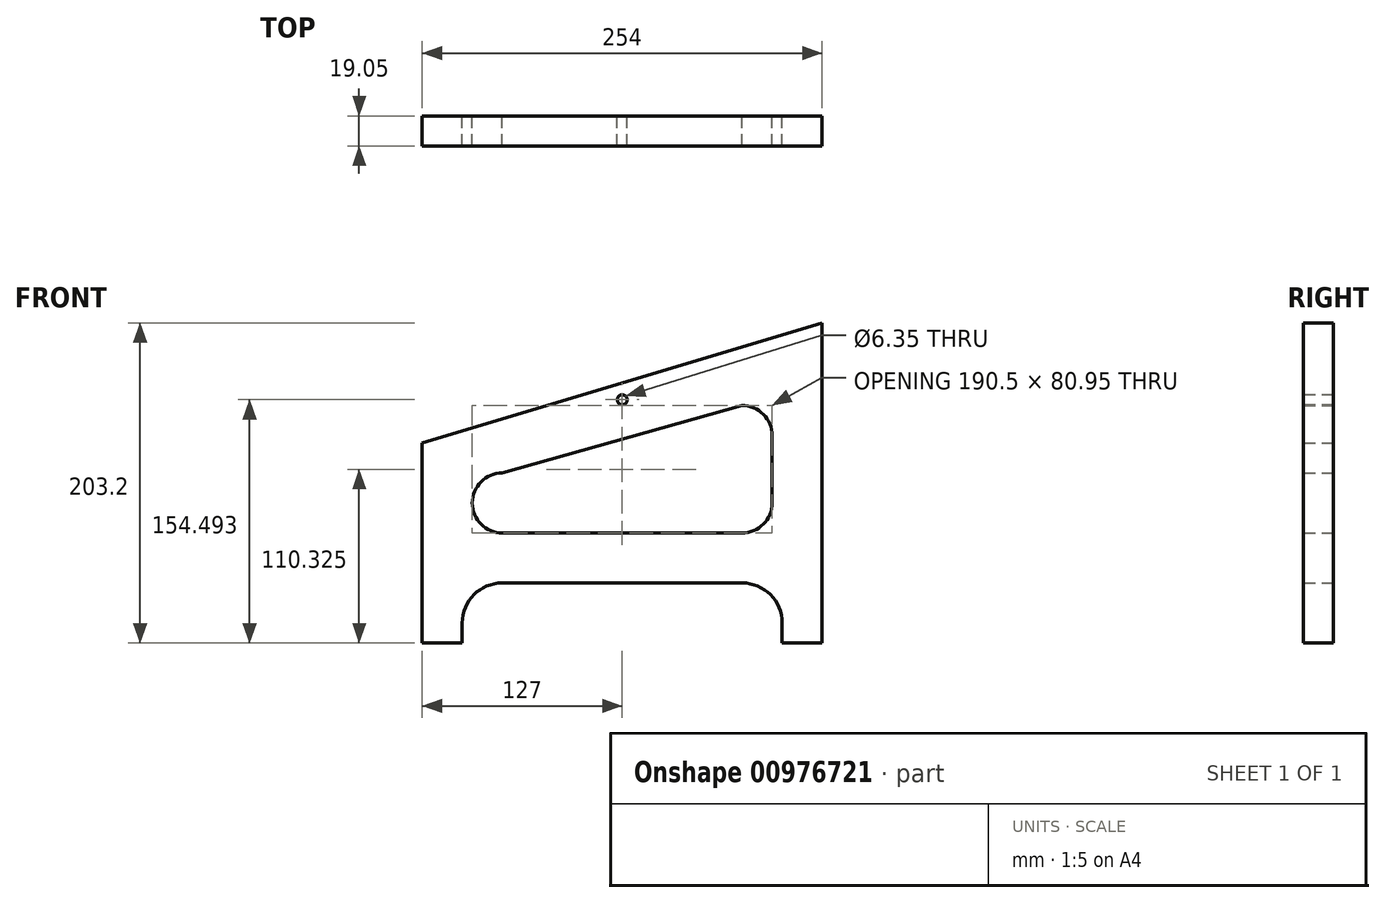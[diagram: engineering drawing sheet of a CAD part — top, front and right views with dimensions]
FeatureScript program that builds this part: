
annotation { "Feature Type Name" : "Feature", "Feature Type Description" : "" }
export const myFeature = defineFeature(function(context is Context, id is Id, definition is map)
    precondition{}
    {
        {
            var Q0;
            Q0=qCreatedBy(makeId("Front.planeOp"),FACE);
            var sketch = newSketch(context, id + "F0", { "sketchPlane" : qUnion([Q0])});
            skLineSegment(sketch, "E0", {"start": v(0, 0) * mm, "end": v(254, 0) * mm});
            skLineSegment(sketch, "E1", {"start": v(254, 0) * mm, "end": v(254, 203.2) * mm});
            skLineSegment(sketch, "E2", {"start": v(0, 0) * mm, "end": v(0, 127) * mm});
            skLineSegment(sketch, "E3", {"start": v(0, 127) * mm, "end": v(254, 203.2) * mm});
            skPoint(sketch, "E4", {"position": v(203.2, 12.7) * mm});
            skPoint(sketch, "E5", {"position": v(50.8, 12.7) * mm});
            skArc(sketch, "E6", {"start": v(50.8, 38.1) * mm, "mid": v(32.84, 30.66) * mm, "end": v(25.4, 12.7) * mm});
            skArc(sketch, "E7", {"start": v(228.6, 12.7) * mm, "mid": v(221.16, 30.66) * mm, "end": v(203.2, 38.1) * mm});
            skLineSegment(sketch, "E8", {"start": v(228.6, 12.7) * mm, "end": v(228.6, 0) * mm});
            skLineSegment(sketch, "E9", {"start": v(25.4, 12.7) * mm, "end": v(25.4, 0) * mm});
            skLineSegment(sketch, "E10", {"start": v(203.2, 38.1) * mm, "end": v(50.8, 38.1) * mm});
            skPoint(sketch, "E11.positionSnap0", {"position": v(127, 38.1) * mm});
            skPoint(sketch, "E12", {"position": v(127, 154.5) * mm});
            skPoint(sketch, "E12.positionSnap0", {"position": v(127, 165.1) * mm});
            skCircle(sketch, "E13", {"center": v(127, 154.5) * mm, "radius": 3.18 * mm});
            skPoint(sketch, "E14", {"position": v(203.2, 88.9) * mm});
            skPoint(sketch, "E15", {"position": v(203.2, 131.75) * mm});
            skPoint(sketch, "E16", {"position": v(50.8, 88.9) * mm});
            skArc(sketch, "E17", {"start": v(203.2, 69.85) * mm, "mid": v(216.67, 75.43) * mm, "end": v(222.25, 88.9) * mm});
            skArc(sketch, "E18", {"start": v(222.25, 131.75) * mm, "mid": v(216.67, 145.22) * mm, "end": v(203.2, 150.8) * mm});
            skArc(sketch, "E19", {"start": v(31.75, 88.9) * mm, "mid": v(37.33, 75.43) * mm, "end": v(50.8, 69.85) * mm});
            skArc(sketch, "E20", {"start": v(50.8, 107.95) * mm, "mid": v(37.33, 102.37) * mm, "end": v(31.75, 88.9) * mm});
            skLineSegment(sketch, "E21", {"start": v(222.25, 88.9) * mm, "end": v(222.25, 131.75) * mm});
            skLineSegment(sketch, "E22", {"start": v(203.2, 150.8) * mm, "end": v(50.8, 107.95) * mm});
            skLineSegment(sketch, "E23", {"start": v(31.75, 88.9) * mm, "end": v(31.75, 88.9) * mm});
            skLineSegment(sketch, "E24", {"start": v(50.8, 69.85) * mm, "end": v(203.2, 69.85) * mm});
            skSolve(sketch);
        }
        {
            var Q0;
            {var subQ4=sQuery(id+"F0.wireOp",EDGE,"E1");Q0=makeQuery(id+"F0.imprint","IMPRINT",FACE,{"disambiguationData":[TD([[makeQuery(id+"F0.imprint","IMPRINT",EDGE,{"derivedFrom":subQ4}),1.0]])]});}
            extrude(context, id + "F1", {"entities" : qUnion([Q0]), "depth" : 19.05 * mm, "offsetDistance" : 25.4 * mm});
        }
    });
